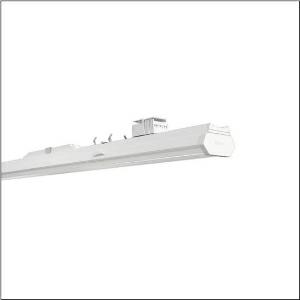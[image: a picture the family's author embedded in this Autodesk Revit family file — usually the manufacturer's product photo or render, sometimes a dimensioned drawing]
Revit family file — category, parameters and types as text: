
# Revit family: licross_21_protected_mo_52tp12dn4a5g3s
name_source: partatom
category: Lighting Fixtures
units: mm (PartAtom-declared; Revit-internal decimal feet)

## family parameters
Cut with Voids When Loaded = No
Host = Face
Light Source = No
Part Type = Normal
Room Calculation Point = No
Round Connector Dimension = Use Diameter
Shared = No

## types (1)
- --- (1 x LED, 940 lm, 6.8 W, 4000K)
    Apparent Load = 7 VA
    CIE Flux Codes = 73 92 98 99 100
    Color Rendering = 80
    Color Temperature = 4000K
    Default Elevation = 1800 mm
    Description = Licross 21 Protected MO, luminaire insert, of sheet steel, galvanised, coil coated, white, length: 1.500mm, width: 90mm, height: 103mm, LED rated luminous flux: 10.700lm, light colour: 840, SDCM (Standard Deviation of Colour Matching)MacAdam ≤ 3 SDCM (initial), control gear: DALI 2 (for two DALI lines), with plug, 6-pole, with phase selection, for trunking rail, 14-core, mains connection: 220..240V, AC, 50/60Hz, rated input power: 66W, for trunking rail, 14-core, internal wiring halogen-free, for emergency light function, converter,control gear: single battery element, battery: LiFePO4, 9Ah, primary light control with lens, of plastic, primary optical cover: cover, of PMMA, light emission: direct distribution, primary light characteristic: symmetric, protection rating (complete): IP64, insulation class (complete): insulation class I (protective earthing), certification: CE, UKCA, protection symbol: D if used in an environment with conductive dust loads with corresponding accessories, impact resistance: IK06, permissible ambient temperature for indoor applications: +5..+35°C, standard: EN 60598-2-22, LABS conformity tested according to VDMA 24364:2018-05, reducing of maximum allowable ambient temperature of 5°C with ceiling mounting, corresponds to IFS (International Featured Standards) requirements for safety and quality in the food industry, The light source and the operating device comply with the requirements of the Ecodesign Regulation (EU) 2019/2020 and are replaceable in accordance with this regulation, packaging unit: 1 piece
    Height = 92 mm
    Lamp = 1 x LED
    Lamp Light Flux = 940 lm
    Lamp Power = 6.8 W
    Lamp count = 1
    Length = 1500 mm
    Luminous efficacy = 138 lm/W
    Manufacturer = Siteco
    ModVariant = No
    Model = 52TP12DN4A5G3S
    Mounting Place = Ceiling
    Mounting Type = Pendant
    Number of Poles = 1
    OnlyDefault = Yes
    Power Factor = 1
    Product Name = Licross 21 Protected MO
    Product group = luminaire insert | ceiling pendant
    ProductGroupID = 901
    Protection Class = Protection class I
    Protection Degree = IP 64
    RLX_Detail_Level = 1
    RLX_Emergency_Light_Flux = 0 lm
    RLX_Emergency_Type = 0
    RLX_Emergency_Type_DB = No
    RlxData = <blob elided: 25133 chars, md5=ae6ba0fc>
    Socket = socket
    Standby Power = 0 W
    System Light Flux = 940 lm
    System Power = 7 W
    Type Comments = : emergency light operation: 3 h
    Type Image = l_1256148.jpg
    URL = http://relux.com
    VarID = @adj_110881
    Voltage = 0 V
    Weight = 0.00 kg
    Width = 88 mm

## geometry (parser evidence)
native form markers: Blend x4, Sweep x9
no freeform markers — native parametric forms only
